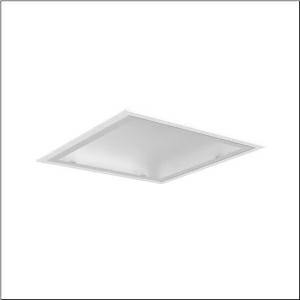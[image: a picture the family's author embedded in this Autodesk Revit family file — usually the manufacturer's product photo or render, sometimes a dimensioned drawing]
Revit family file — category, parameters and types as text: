
# Revit family: mira_r__11_51fr127a471a_dfe6
name_source: partatom
category: Lighting Fixtures
units: mm (PartAtom-declared; Revit-internal decimal feet)

## family parameters
Cut with Voids When Loaded = No
Host = Face
Light Source = No
Part Type = Normal
Room Calculation Point = No
Round Connector Dimension = Use Diameter
Shared = No

## types (1)
- Mira® 11 (1 x LED, 7290 lm, 66 W, 4000K)
    Apparent Load = 66 VA
    CIE Flux Codes = 51 82 97 100 100
    Color Rendering = 80
    Color Temperature = 4000K
    Default Elevation = 1800 mm
    Description = Mira® 11, clean room luminaire, primary light control with reflector, primary optical cover: cover, of toughened safety glass, light emission: direct distribution, primary light characteristic: symmetric, installation type: recessed, LED, rated luminous flux: 7.290lm, luminous efficacy: 111lm/W, light colour: 840, colour temperature: 4000K, control gear: ON/OFF, with terminal, 3-pole, max. 2.5mm², mains connection: 230V, AC, 50/60Hz, rated input power: 66W, luminaire housing, of sheet steel, coated, pure white (RAL 9010), with concealed magnets, module: M625, length: 623mm, width: 623mm, height: 90mm, protection rating (complete): IP65, insulation class (complete): insulation class I (protective earthing), certification: CE, UKCA, permissible operating ambient temperature: -5..+40°C, standard: EN 50419, packaging unit: 1 piece
    Height = 0 mm  [stored 0 ft]
    Lamp = 1 x LED
    Lamp Light Flux = 7290 lm
    Lamp Power = 66 W
    Lamp count = 1
    Length = 625 mm
    Luminous efficacy = 110 lm/W
    Manufacturer = Siteco
    ModVariant = No
    Model = 51FR127A471A
    Mounting Place = Ceiling
    Mounting Type = Recessed
    Number of Poles = 1
    OnlyDefault = Yes
    Power Factor = 1
    Product Name = Mira® 11
    Product group = clean room luminaire | ceiling recessed
    ProductGroupID = 402
    Protection Class = Protection class I
    Protection Degree = IP 65
    RLX_Detail_Level = 1
    RLX_Emergency_Light_Flux = 0 lm
    RLX_Emergency_Type = 0
    RLX_Emergency_Type_DB = No
    RlxData = <blob elided: 19261 chars, md5=cff940fd>
    Socket = socket
    Standby Power = 0 W
    System Light Flux = 7290 lm
    System Power = 66 W
    Type Comments = Product without accessories
    Type Image = l_1006636.jpg
    URL = http://relux.com
    VarID = ---
    Voltage = 0 V
    Weight = 0.00 kg
    Width = 625 mm

note: [stored X ft] marks values corroborated as IEEE doubles in the binary element streams (Revit-internal decimal feet)

## geometry (parser evidence)
native form markers: Blend x4, Sweep x10
no freeform markers — native parametric forms only
